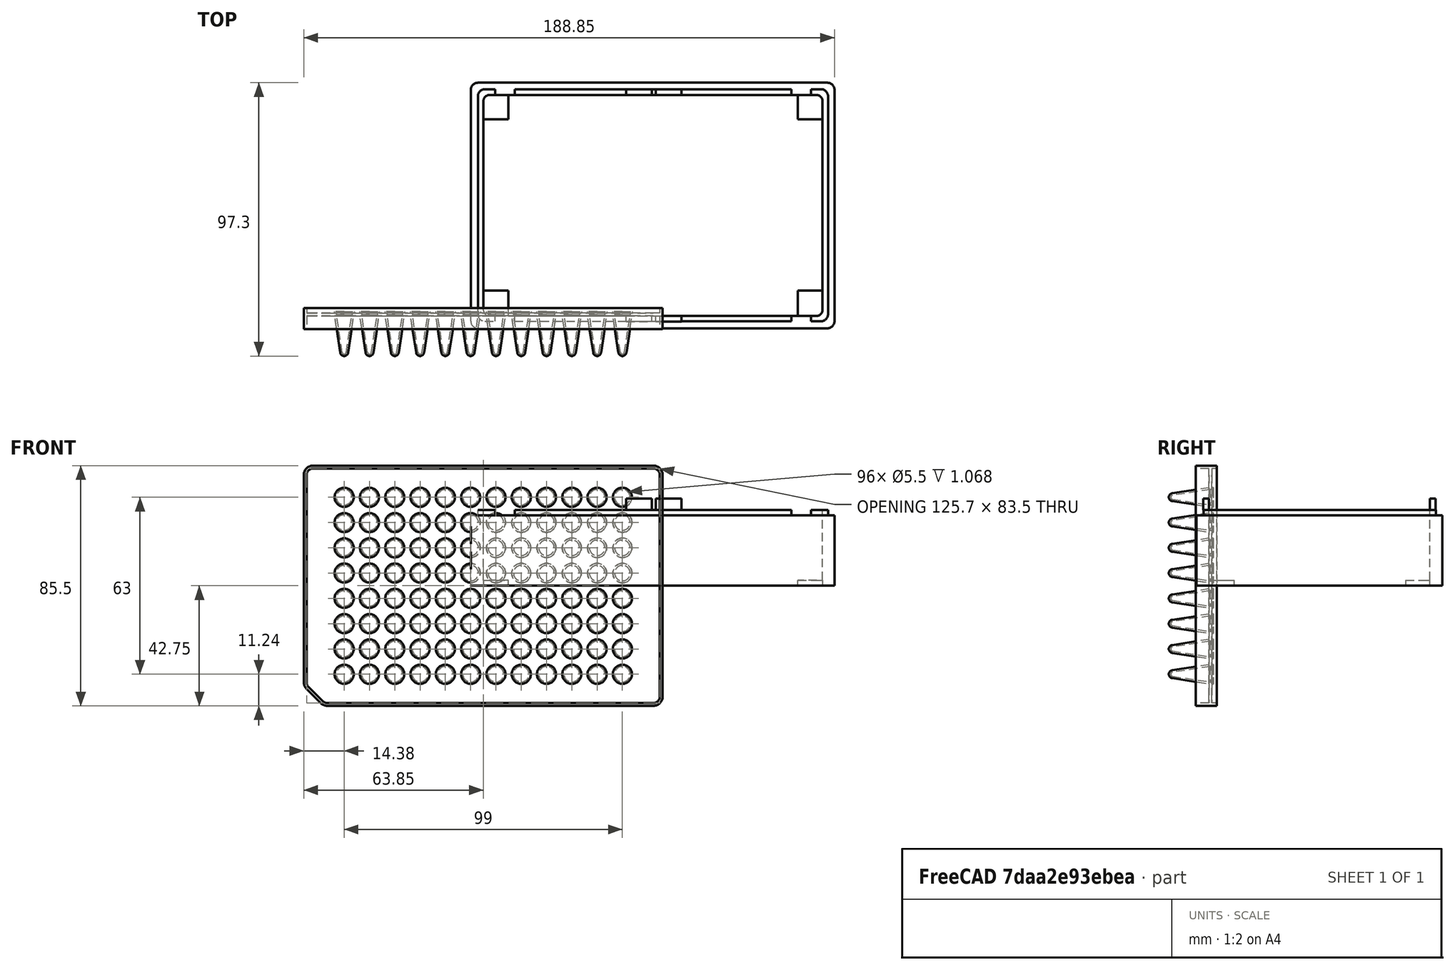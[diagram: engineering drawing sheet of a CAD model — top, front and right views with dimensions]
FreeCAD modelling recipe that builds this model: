
FCSTD DOCUMENT  (FreeCAD 0.18R16110 (Git))
Label: 96-well-rack
License: All rights reserved
LicenseURL: http://en.wikipedia.org/wiki/All_rights_reserved
objects: Part::Box×15, Part::Cut×7, Part::Fillet×3, Part::MultiFuse×2, Spreadsheet::Sheet×1, Mesh::Feature×1, Part::Feature×1, App::Part×1
note: 28 computed .brp shape members not serialized (recipe doc carries the construction recipe); baked Part::Feature solids carry a one-line shape summary decoded from their .brp

FEATURE [Spreadsheet::Sheet] Spreadsheet
  cells = A1=0.2; B1=Tolerance; A2=83; B2=width; A3=125; B3=length; A4=4; B4=thickness wall; A5=25; B5=height; A7=2; B7=absatz; A9=Führung; A10=20; B10=Länge; A11=4; B11=höhe
FEATURE [Part::Box] Box  label="Quader"
  AttacherType = Attacher::AttachEngine3D
  Height = 27
  Length = 120.6
  Placement = pos=(0.1,0,0) rot=(0,0,1;0rad)
  Width = 78.6
  expr: Placement.Base.x = Spreadsheet.A1 / 2
  expr: Height = Spreadsheet.A5 + Spreadsheet.A7
  expr: Width = Spreadsheet.A2 - 2 * Spreadsheet.A4 / 2 - 2 * Spreadsheet.A1
  expr: Length = Spreadsheet.A3 - 2 * Spreadsheet.A4 / 2 - 2 * Spreadsheet.A1
FEATURE [Part::Box] Box001  label="Quader001"
  AttacherType = Attacher::AttachEngine3D
  Height = 25
  Length = 129.4
  Placement = pos=(-4.4,-4.4,0) rot=(0,0,1;0rad)
  Width = 87.4
  expr: Placement.Base.y = -(Spreadsheet.A4 / 2 + Spreadsheet.A1) * 2
  expr: Placement.Base.x = -(Spreadsheet.A4 / 2 + Spreadsheet.A1) * 2
  expr: Height = Spreadsheet.A5
  expr: Width = Spreadsheet.A2 + 2 * Spreadsheet.A4 / 2 + 2 * Spreadsheet.A1
  expr: Length = Spreadsheet.A3 + 2 * Spreadsheet.A4 / 2 + 2 * Spreadsheet.A1
FEATURE [Part::Box] Box002  label="Quader002"
  AttacherType = Attacher::AttachEngine3D
  Height = 2
  Length = 124.6
  Placement = pos=(-1.9,-1.9,25) rot=(0,0,1;0rad)
  Width = 82.6
  expr: Placement.Base.y = -Spreadsheet.A4 / 2 + Spreadsheet.A1 / 2
  expr: Placement.Base.x = -Spreadsheet.A4 / 2 + Spreadsheet.A1 / 2
  expr: Placement.Base.z = Spreadsheet.A5
  expr: Height = Spreadsheet.A7
  expr: Width = Spreadsheet.A2 - 2 * Spreadsheet.A1
  expr: Length = Spreadsheet.A3 - 2 * Spreadsheet.A1
FEATURE [Part::Box] Box004  label="Quader004"
  AttacherType = Attacher::AttachEngine3D
  Height = 4
  Length = 19.6
  Placement = pos=(50.9,-2,27) rot=(0,0,1;0rad)
  Width = 2
  expr: Placement.Base.y = -Spreadsheet.A4 / 2
  expr: Placement.Base.x = +Spreadsheet.A1 - Spreadsheet.A4 / 2 + Spreadsheet.A3 / 2 - (Spreadsheet.A10 - 2 * Spreadsheet.A1) / 2
  expr: Placement.Base.z = Spreadsheet.A5 + Spreadsheet.A7
  expr: Height = Spreadsheet.A11
  expr: Width = Spreadsheet.A4 / 2
  expr: Length = Spreadsheet.A10 - 2 * Spreadsheet.A1
FEATURE [Part::Box] Box005  label="Quader005"
  AttacherType = Attacher::AttachEngine3D
  Height = 4
  Length = 19.6
  Placement = pos=(50.9,78.6,27) rot=(0,0,1;0rad)
  Width = 2
  expr: Placement.Base.y = -Spreadsheet.A4 - Spreadsheet.A1 * 2 + Spreadsheet.A2
  expr: Placement.Base.x = +Spreadsheet.A1 - Spreadsheet.A4 / 2 + Spreadsheet.A3 / 2 - (Spreadsheet.A10 - 2 * Spreadsheet.A1) / 2
  expr: Placement.Base.z = Spreadsheet.A5 + Spreadsheet.A7
  expr: Height = Spreadsheet.A11
  expr: Width = Spreadsheet.A4 / 2
  expr: Length = Spreadsheet.A10 - 2 * Spreadsheet.A1
FEATURE [Part::Fillet] Fillet
  Base = -> Box
  Edges = 4 edges r=2: [Edge1,Edge3,Edge5,Edge7]
FEATURE [Part::Fillet] Fillet001
  Base = -> Box001
  Edges = 4 edges r=2.5: [Edge1,Edge3,Edge5,Edge7]
FEATURE [Part::Fillet] Fillet002
  Base = -> Box002
  Edges = 4 edges r=2.5: [Edge1,Edge3,Edge5,Edge7]
FEATURE [Part::Box] Box006  label="Quader006"
  AttacherType = Attacher::AttachEngine3D
  Height = 4
  Length = 1.4
  Placement = pos=(60,-2,27) rot=(0,0,1;0rad)
  Width = 2
  expr: Placement.Base.z = Spreadsheet.A5 + Spreadsheet.A7
  expr: Height = Spreadsheet.A11
  expr: Placement.Base.y = -Spreadsheet.A4 / 2
  expr: Placement.Base.x = +Spreadsheet.A1 - Spreadsheet.A4 / 2 + Spreadsheet.A3 / 2 - (1 + 2 * Spreadsheet.A1) / 2
  expr: Width = Spreadsheet.A4 / 2
  expr: Length = 1 + 2 * Spreadsheet.A1
FEATURE [Part::Box] Box007  label="Quader007"
  AttacherType = Attacher::AttachEngine3D
  Height = 4
  Length = 1.4
  Placement = pos=(60,78.6,27) rot=(0,0,1;0rad)
  Width = 2
  expr: Placement.Base.z = Spreadsheet.A5 + Spreadsheet.A7
  expr: Height = Spreadsheet.A11
  expr: Placement.Base.y = -Spreadsheet.A4 - Spreadsheet.A1 * 2 + Spreadsheet.A2
  expr: Placement.Base.x = +Spreadsheet.A1 - Spreadsheet.A4 / 2 + Spreadsheet.A3 / 2 - (1 + 2 * Spreadsheet.A1) / 2
  expr: Width = Spreadsheet.A4 / 2
  expr: Length = 1 + 2 * Spreadsheet.A1
FEATURE [Part::Box] Box008  label="Quader008"
  AttacherType = Attacher::AttachEngine3D
  Height = 2
  Length = 7
  Placement = pos=(4.2,-2,25) rot=(0,0,1;0rad)
  Width = 2.5
  expr: Placement.Base.x = -Spreadsheet.A4 / 2 + Spreadsheet.A1 + 6
  expr: Placement.Base.y = -Spreadsheet.A4 / 2
  expr: Placement.Base.z = Spreadsheet.A5 + Spreadsheet.A7 - Spreadsheet.A4 / 2
FEATURE [Part::Box] Box009  label="Quader009"
  AttacherType = Attacher::AttachEngine3D
  Height = 2
  Length = 7
  Placement = pos=(109.6,-2,25) rot=(0,0,1;0rad)
  Width = 2.5
  expr: Placement.Base.x = -Spreadsheet.A4 + Spreadsheet.A1 * 3 - 6 * 2 + Spreadsheet.A3
  expr: Placement.Base.y = -Spreadsheet.A4 / 2
  expr: Placement.Base.z = Spreadsheet.A5 + Spreadsheet.A7 - Spreadsheet.A4 / 2
FEATURE [Part::Box] Box010  label="Quader010"
  AttacherType = Attacher::AttachEngine3D
  Height = 2
  Length = 7
  Placement = pos=(109.6,78.6,25) rot=(0,0,1;0rad)
  Width = 2.5
  expr: Placement.Base.x = -Spreadsheet.A4 + Spreadsheet.A1 * 3 - 6 * 2 + Spreadsheet.A3
  expr: Placement.Base.y = -Spreadsheet.A4 - Spreadsheet.A1 * 2 + Spreadsheet.A2
  expr: Placement.Base.z = Spreadsheet.A5 + Spreadsheet.A7 - Spreadsheet.A4 / 2
FEATURE [Part::Box] Box011  label="Quader011"
  AttacherType = Attacher::AttachEngine3D
  Height = 2
  Length = 7
  Placement = pos=(4.2,78.4,25) rot=(0,0,1;0rad)
  Width = 2.4
  expr: Width = 2 + Spreadsheet.A1 * 2
  expr: Placement.Base.x = -Spreadsheet.A4 / 2 + Spreadsheet.A1 + 6
  expr: Placement.Base.y = -Spreadsheet.A4 - Spreadsheet.A1 * 3 + Spreadsheet.A2
  expr: Placement.Base.z = Spreadsheet.A5 + Spreadsheet.A7 - Spreadsheet.A4 / 2
FEATURE [Part::MultiFuse] Fusion
  Shapes = -> [Fillet001,Fillet002,Box004,Box005]
FEATURE [Part::Cut] Cut
  Base = -> Fusion
  Tool = -> Box006
FEATURE [Part::Cut] Cut001
  Base = -> Cut
  Tool = -> Box007
FEATURE [Part::Cut] Cut002
  Base = -> Cut001
  Tool = -> Box008
FEATURE [Part::Cut] Cut003
  Base = -> Cut002
  Tool = -> Box009
FEATURE [Part::Cut] Cut004
  Base = -> Cut003
  Tool = -> Box010
FEATURE [Part::Cut] Cut005
  Base = -> Cut004
  Tool = -> Box011
FEATURE [Part::Cut] Cut006
  Base = -> Cut005
  Tool = -> Fillet
FEATURE [Part::Box] Box012  label="Quader012"
  AttacherType = Attacher::AttachEngine3D
  Height = 2
  Length = 10
  Placement = pos=(-1,-1,0) rot=(0,0,1;0rad)
  Width = 10
FEATURE [Part::Box] Box013  label="Quader013"
  AttacherType = Attacher::AttachEngine3D
  Height = 2
  Length = 10
  Placement = pos=(112,70,0) rot=(0,0,1;0rad)
  Width = 10
FEATURE [Part::Box] Box014  label="Quader014"
  AttacherType = Attacher::AttachEngine3D
  Height = 2
  Length = 10
  Placement = pos=(-1,70,0) rot=(0,0,1;0rad)
  Width = 10
FEATURE [Part::Box] Box015  label="Quader015"
  AttacherType = Attacher::AttachEngine3D
  Height = 2
  Length = 10
  Placement = pos=(112,-1,0) rot=(0,0,1;0rad)
  Width = 10
FEATURE [Part::MultiFuse] Fusion001  label="96-well-rack"
  Shapes = -> [Box012,Box013,Box014,Box015,Cut006]
FEATURE [Mesh::Feature] Mesh  label="96-well-rack(Meshed)"
FEATURE [Part::Feature] Part__Feature  label="Default"
  shape: bbox 127.7 x 17.1 x 85.5 mm, 706 faces (baked)
FEATURE [App::Part] _6_well_plate  label="96_well_plate"
  Group = -> [Part__Feature]
  License = CC BY 3.0
  LicenseURL = http://creativecommons.org/licenses/by/3.0/
  Origin = -> Origin
  Placement = pos=(61,39,31) rot=(1,0,0;1.5708rad)
